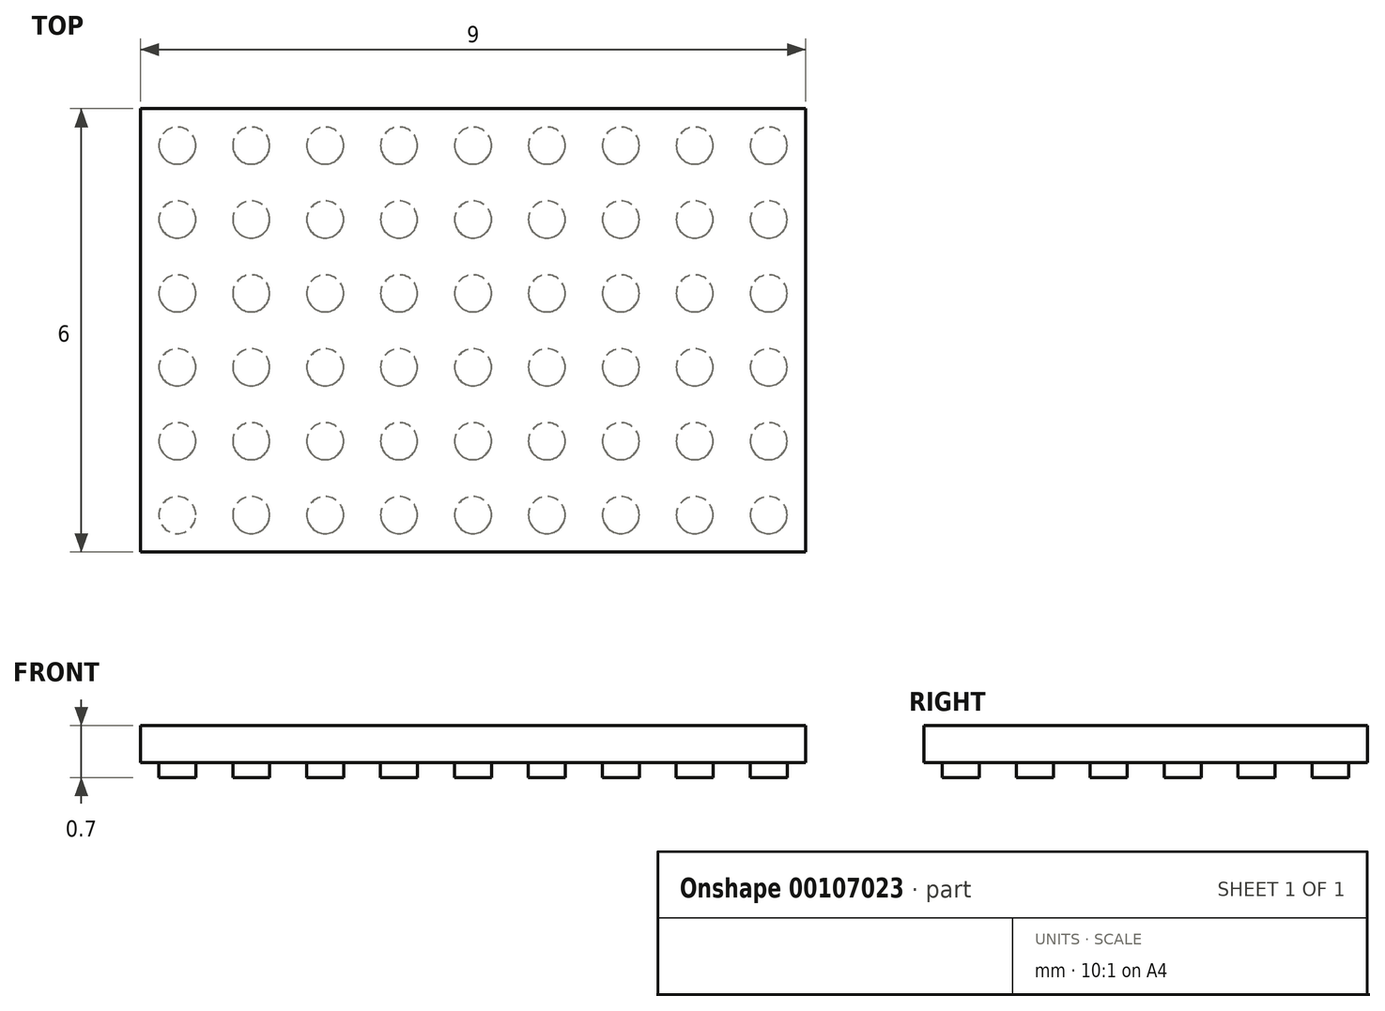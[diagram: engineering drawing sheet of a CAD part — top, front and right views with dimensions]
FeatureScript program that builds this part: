
annotation { "Feature Type Name" : "Feature", "Feature Type Description" : "" }
export const myFeature = defineFeature(function(context is Context, id is Id, definition is map)
    precondition{}
    {
        {
            var Q0;
            Q0=qCreatedBy(makeId("Top.planeOp"),FACE);
            var sketch = newSketch(context, id + "F0", { "sketchPlane" : qUnion([Q0])});
            skLineSegment(sketch, "E0.bottom", {"start": v(0, 0) * mm, "end": v(9, 0) * mm});
            skLineSegment(sketch, "E0.top", {"start": v(0, 6) * mm, "end": v(9, 6) * mm});
            skLineSegment(sketch, "E0.left", {"start": v(0, 0) * mm, "end": v(0, 6) * mm});
            skLineSegment(sketch, "E0.right", {"start": v(9, 0) * mm, "end": v(9, 6) * mm});
            skSolve(sketch);
        }
        {
            var Q0;
            Q0 = qSketchRegion(id + "F0", true);
            extrude(context, id + "F1", {"entities" : qUnion([Q0]), "depth" : .5 * mm});
        }
        {
            var Q0;
            Q0=makeQuery(id+"F1.opExtrude","CAP_FACE",FACE,{"disambiguationData":[OSD([sQuery(id+"F0.wireOp",EDGE,"E0.bottom"),sQuery(id+"F0.wireOp",EDGE,"E0.top"),sQuery(id+"F0.wireOp",EDGE,"E0.left"),sQuery(id+"F0.wireOp",EDGE,"E0.right")])],"isStart":true});
            var sketch = newSketch(context, id + "F2", { "sketchPlane" : qUnion([Q0])});
            skCircle(sketch, "E1", {"center": v(0.5, -0.5) * mm, "radius": 0.25 * mm});
            skCircle(sketch, "E2.1.0.0", {"center": v(1.5, -0.5) * mm, "radius": 0.25 * mm});
            skCircle(sketch, "E2.2.0.0", {"center": v(2.5, -0.5) * mm, "radius": 0.25 * mm});
            skCircle(sketch, "E2.3.0.0", {"center": v(3.5, -0.5) * mm, "radius": 0.25 * mm});
            skCircle(sketch, "E2.4.0.0", {"center": v(4.5, -0.5) * mm, "radius": 0.25 * mm});
            skCircle(sketch, "E2.5.0.0", {"center": v(5.5, -0.5) * mm, "radius": 0.25 * mm});
            skCircle(sketch, "E2.6.0.0", {"center": v(6.5, -0.5) * mm, "radius": 0.25 * mm});
            skCircle(sketch, "E2.7.0.0", {"center": v(7.5, -0.5) * mm, "radius": 0.25 * mm});
            skCircle(sketch, "E2.8.0.0", {"center": v(8.5, -0.5) * mm, "radius": 0.25 * mm});
            skLineSegment(sketch, "E2.direction1", {"start": v(0.5, -0.5) * mm, "end": v(1.5, -0.5) * mm, "construction": true});
            skCircle(sketch, "E3.0.1.3", {"center": v(8.5, -1.5) * mm, "radius": 0.25 * mm});
            skCircle(sketch, "E3.0.1.4", {"center": v(7.5, -1.5) * mm, "radius": 0.25 * mm});
            skCircle(sketch, "E3.0.1.5", {"center": v(6.5, -1.5) * mm, "radius": 0.25 * mm});
            skCircle(sketch, "E3.0.1.6", {"center": v(5.5, -1.5) * mm, "radius": 0.25 * mm});
            skCircle(sketch, "E3.0.1.7", {"center": v(4.5, -1.5) * mm, "radius": 0.25 * mm});
            skCircle(sketch, "E3.0.1.8", {"center": v(3.5, -1.5) * mm, "radius": 0.25 * mm});
            skCircle(sketch, "E3.0.1.9", {"center": v(2.5, -1.5) * mm, "radius": 0.25 * mm});
            skLineSegment(sketch, "E3.0.1.10", {"start": v(0.5, -1.5) * mm, "end": v(1.5, -1.5) * mm, "construction": true});
            skCircle(sketch, "E3.0.1.11", {"center": v(1.5, -1.5) * mm, "radius": 0.25 * mm});
            skCircle(sketch, "E3.0.1.12", {"center": v(0.5, -1.5) * mm, "radius": 0.25 * mm});
            skCircle(sketch, "E3.0.2.3", {"center": v(8.5, -2.5) * mm, "radius": 0.25 * mm});
            skCircle(sketch, "E3.0.2.4", {"center": v(7.5, -2.5) * mm, "radius": 0.25 * mm});
            skCircle(sketch, "E3.0.2.5", {"center": v(6.5, -2.5) * mm, "radius": 0.25 * mm});
            skCircle(sketch, "E3.0.2.6", {"center": v(5.5, -2.5) * mm, "radius": 0.25 * mm});
            skCircle(sketch, "E3.0.2.7", {"center": v(4.5, -2.5) * mm, "radius": 0.25 * mm});
            skCircle(sketch, "E3.0.2.8", {"center": v(3.5, -2.5) * mm, "radius": 0.25 * mm});
            skCircle(sketch, "E3.0.2.9", {"center": v(2.5, -2.5) * mm, "radius": 0.25 * mm});
            skLineSegment(sketch, "E3.0.2.10", {"start": v(0.5, -2.5) * mm, "end": v(1.5, -2.5) * mm, "construction": true});
            skCircle(sketch, "E3.0.2.11", {"center": v(1.5, -2.5) * mm, "radius": 0.25 * mm});
            skCircle(sketch, "E3.0.2.12", {"center": v(0.5, -2.5) * mm, "radius": 0.25 * mm});
            skCircle(sketch, "E3.0.3.3", {"center": v(8.5, -3.5) * mm, "radius": 0.25 * mm});
            skCircle(sketch, "E3.0.3.4", {"center": v(7.5, -3.5) * mm, "radius": 0.25 * mm});
            skCircle(sketch, "E3.0.3.5", {"center": v(6.5, -3.5) * mm, "radius": 0.25 * mm});
            skCircle(sketch, "E3.0.3.6", {"center": v(5.5, -3.5) * mm, "radius": 0.25 * mm});
            skCircle(sketch, "E3.0.3.7", {"center": v(4.5, -3.5) * mm, "radius": 0.25 * mm});
            skCircle(sketch, "E3.0.3.8", {"center": v(3.5, -3.5) * mm, "radius": 0.25 * mm});
            skCircle(sketch, "E3.0.3.9", {"center": v(2.5, -3.5) * mm, "radius": 0.25 * mm});
            skLineSegment(sketch, "E3.0.3.10", {"start": v(0.5, -3.5) * mm, "end": v(1.5, -3.5) * mm, "construction": true});
            skCircle(sketch, "E3.0.3.11", {"center": v(1.5, -3.5) * mm, "radius": 0.25 * mm});
            skCircle(sketch, "E3.0.3.12", {"center": v(0.5, -3.5) * mm, "radius": 0.25 * mm});
            skCircle(sketch, "E3.0.4.3", {"center": v(8.5, -4.5) * mm, "radius": 0.25 * mm});
            skCircle(sketch, "E3.0.4.4", {"center": v(7.5, -4.5) * mm, "radius": 0.25 * mm});
            skCircle(sketch, "E3.0.4.5", {"center": v(6.5, -4.5) * mm, "radius": 0.25 * mm});
            skCircle(sketch, "E3.0.4.6", {"center": v(5.5, -4.5) * mm, "radius": 0.25 * mm});
            skCircle(sketch, "E3.0.4.7", {"center": v(4.5, -4.5) * mm, "radius": 0.25 * mm});
            skCircle(sketch, "E3.0.4.8", {"center": v(3.5, -4.5) * mm, "radius": 0.25 * mm});
            skCircle(sketch, "E3.0.4.9", {"center": v(2.5, -4.5) * mm, "radius": 0.25 * mm});
            skLineSegment(sketch, "E3.0.4.10", {"start": v(0.5, -4.5) * mm, "end": v(1.5, -4.5) * mm, "construction": true});
            skCircle(sketch, "E3.0.4.11", {"center": v(1.5, -4.5) * mm, "radius": 0.25 * mm});
            skCircle(sketch, "E3.0.4.12", {"center": v(0.5, -4.5) * mm, "radius": 0.25 * mm});
            skCircle(sketch, "E3.0.5.3", {"center": v(8.5, -5.5) * mm, "radius": 0.25 * mm});
            skCircle(sketch, "E3.0.5.4", {"center": v(7.5, -5.5) * mm, "radius": 0.25 * mm});
            skCircle(sketch, "E3.0.5.5", {"center": v(6.5, -5.5) * mm, "radius": 0.25 * mm});
            skCircle(sketch, "E3.0.5.6", {"center": v(5.5, -5.5) * mm, "radius": 0.25 * mm});
            skCircle(sketch, "E3.0.5.7", {"center": v(4.5, -5.5) * mm, "radius": 0.25 * mm});
            skCircle(sketch, "E3.0.5.8", {"center": v(3.5, -5.5) * mm, "radius": 0.25 * mm});
            skCircle(sketch, "E3.0.5.9", {"center": v(2.5, -5.5) * mm, "radius": 0.25 * mm});
            skLineSegment(sketch, "E3.0.5.10", {"start": v(0.5, -5.5) * mm, "end": v(1.5, -5.5) * mm, "construction": true});
            skCircle(sketch, "E3.0.5.11", {"center": v(1.5, -5.5) * mm, "radius": 0.25 * mm});
            skCircle(sketch, "E3.0.5.12", {"center": v(0.5, -5.5) * mm, "radius": 0.25 * mm});
            skLineSegment(sketch, "E3.direction2", {"start": v(0.5, -0.5) * mm, "end": v(0.5, -1.5) * mm, "construction": true});
            skSolve(sketch);
        }
        {
            var Q0;
            Q0 = qSketchRegion(id + "F2", true);
            extrude(context, id + "F3", {"entities" : qUnion([Q0]), "operationType" : NewBodyOperationType.ADD, "depth" : .2 * mm});
        }
    });
